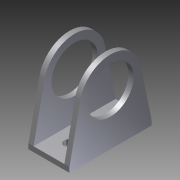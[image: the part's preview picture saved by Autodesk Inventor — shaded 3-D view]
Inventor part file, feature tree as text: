
AUTODESK INVENTOR PART (.ipt)
format: ipt  version: 2012 (Build 160160000, 160)  size: 128,512 bytes
history: native  units: in
note: dims shown in document units (in); Inventor stores cm internally (conversion verified against a paired STEP export)
features: extrude x3, sketch x3
ambient origin geometry x8: Origin, YZ Plane, XZ Plane, XY Plane, X Axis, Y Axis, Z Axis, Center Point
bodies: Solid1 (feature_tree)
feature tree (6):
  extrude  "Extrusion1"  Depth=1.0in
  extrude  "Extrusion2"  Depth=0.125in
  extrude  "Extrusion3"  Depth=2.0in TaperAngle=0.0deg
  sketch  "Sketch1"  dims[d0=2.0in d1=1.0in]
  sketch  "Sketch2"  dims[d2=0.125in d3=0.125in]
  sketch  "Sketch3"  dims[d4=0.125in d5=2.0in d6=0.0in d7=1.125in d8=1.0in d9=0.75in d10=2.0in d11=0.0in d12=0.25in d13=0.25in d14=0.5in d15=0.375in d16=0.5in d17=0.375in d18=2.0in d19=0.0in]
